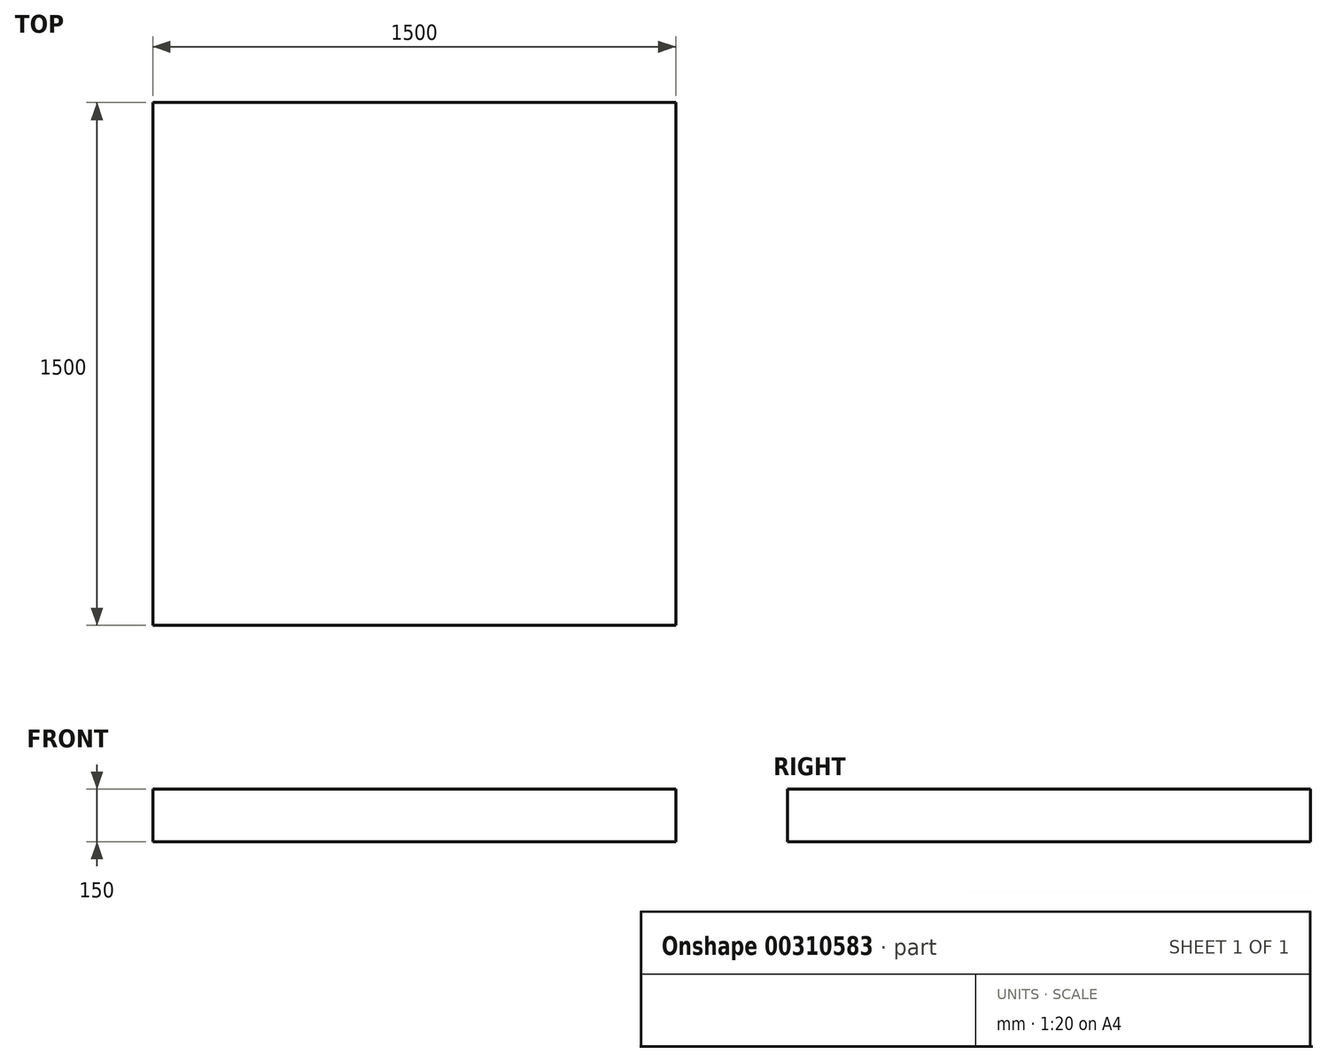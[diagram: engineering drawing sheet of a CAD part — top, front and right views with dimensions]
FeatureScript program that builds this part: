
annotation { "Feature Type Name" : "Feature", "Feature Type Description" : "" }
export const myFeature = defineFeature(function(context is Context, id is Id, definition is map)
    precondition{}
    {
        {
            var Q0;
            Q0=qCreatedBy(makeId("Top.planeOp"),FACE);
            var sketch = newSketch(context, id + "F0", { "sketchPlane" : qUnion([Q0])});
            skLineSegment(sketch, "E0.bottom", {"start": v(-750, 750) * mm, "end": v(750, 750) * mm});
            skLineSegment(sketch, "E0.top", {"start": v(-750, -750) * mm, "end": v(750, -750) * mm});
            skLineSegment(sketch, "E0.left", {"start": v(-750, 750) * mm, "end": v(-750, -750) * mm});
            skLineSegment(sketch, "E0.right", {"start": v(750, 750) * mm, "end": v(750, -750) * mm});
            skPoint(sketch, "E0.middle", {"position": v(0, 0) * mm});
            skLineSegment(sketch, "E1.bottom", {"start": v(0, -820.31) * mm, "end": v(44.12, -820.31) * mm});
            skLineSegment(sketch, "E1.top", {"start": v(0, -820.31) * mm, "end": v(44.12, -820.31) * mm});
            skLineSegment(sketch, "E1.left", {"start": v(0, -820.31) * mm, "end": v(0, -820.31) * mm});
            skLineSegment(sketch, "E1.right", {"start": v(44.12, -820.31) * mm, "end": v(44.12, -820.31) * mm});
            skPoint(sketch, "E1.middle", {"position": v(22.06, -820.31) * mm});
            skPoint(sketch, "E1.cornerSnap0", {"position": v(0, -750) * mm});
            skSolve(sketch);
        }
        {
            var Q0;
            Q0=makeQuery(id+"F0.imprint","IMPRINT",FACE,{"disambiguationData":[TD([[makeQuery(id+"F0.imprint","IMPRINT",EDGE,{"derivedFrom":sQuery(id+"F0.wireOp",EDGE,"E0.bottom")}),-1.0]])]});
            extrude(context, id + "F1", {"entities" : qUnion([Q0]), "depth" : 150 * mm});
        }
    });
